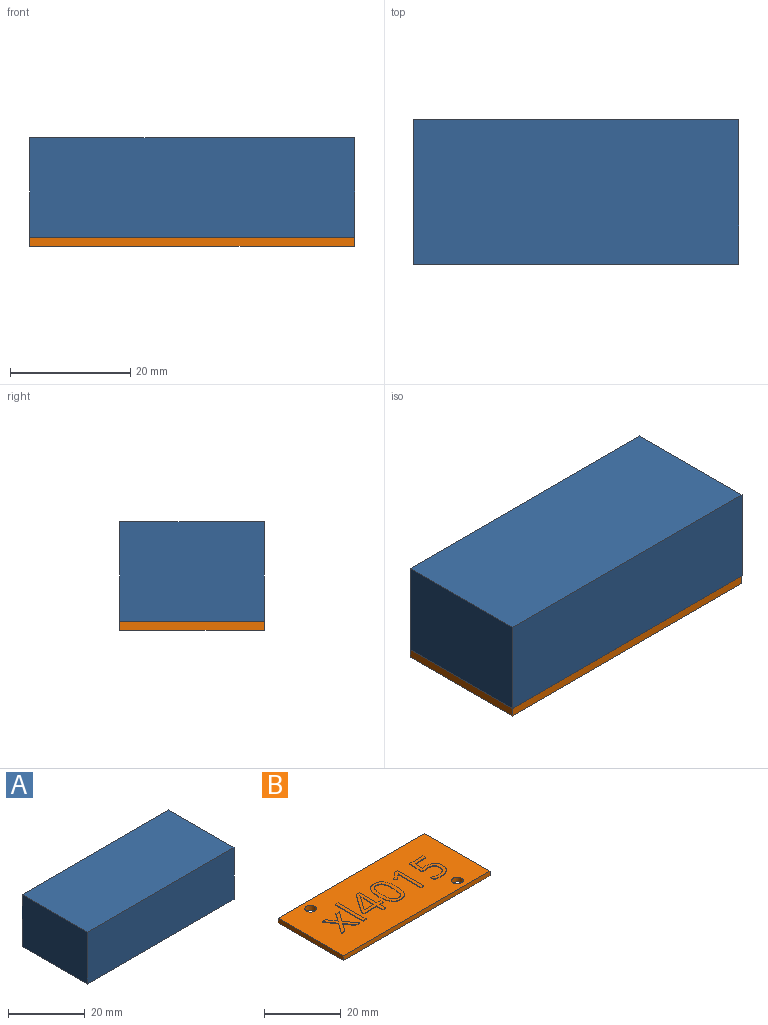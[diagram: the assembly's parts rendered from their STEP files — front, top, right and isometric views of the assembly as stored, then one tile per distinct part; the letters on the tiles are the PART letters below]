
ASSEMBLY  parts=2 mates=1
PART A: 6 faces, bbox 54x24x16.5 mm
  f0: plane 54x16.5mm, normal (0,-1,0), area 891mm2, adj f1,f3,f4,f5
  f1: plane 24x16.5mm, normal (1,0,0), area 396mm2, adj f0,f2,f4,f5
  f2: plane 54x16.5mm, normal (0,1,0), area 891mm2, adj f1,f3,f4,f5
  f3: plane 24x16.5mm, normal (-1,0,0), area 396mm2, adj f0,f2,f4,f5
  f4: plane 54x24mm, normal (0,0,1), area 1296mm2, adj f0,f1,f2,f3
  f5: plane 54x24mm, normal (0,0,-1), area 1296mm2, adj f0,f1,f2,f3
PART B: 93 faces, bbox 54x24x1.7 mm
  f0: plane 54x24mm, normal (0,0,1), area 1136.2mm2, adj f1,f2,f3,f4,f5,f6,f8,f9
  f1: plane 54x1.5mm, normal (0,-1,0), area 81mm2, adj f0,f2,f6,f7
  f2: plane 24x1.5mm, normal (1,0,0), area 36mm2, adj f0,f1,f3,f7
  f3: plane 54x1.5mm, normal (0,1,0), area 81mm2, adj f0,f2,f6,f7
  f4: cylinder r=1.5mm len=3mm, axis (0,0,-1), area 14.1mm2, adj f0,f7
  f5: cylinder r=1.5mm len=3mm, axis (0,0,-1), area 14.1mm2, adj f0,f7
  f6: plane 24x1.5mm, normal (-1,0,0), area 36mm2, adj f0,f1,f3,f7
  f7: plane 54x24mm, normal (0,0,-1), area 1281.9mm2, adj f1,f2,f3,f4,f5,f6
  f8: plane 3.69x2.64mm, normal (-0.81,0.58,0), area 0.9mm2, adj f0,f9,f19,f20
  f9: plane 1.24x0.2mm, normal (0,-1,0), area 0.2mm2, adj f0,f8,f10,f20
  f10: plane 2.92x2.04mm, normal (0.82,-0.57,0), area 0.7mm2, adj f0,f9,f11,f20
  f11: plane 2.92x2.02mm, normal (-0.82,-0.57,0), area 0.7mm2, adj f0,f10,f12,f20
  f12: plane 1.24x0.2mm, normal (0,-1,0), area 0.2mm2, adj f0,f11,f13,f20
  f13: plane 3.69x2.64mm, normal (0.81,0.58,0), area 0.9mm2, adj f0,f12,f14,f20
  f14: plane 3.52x2.51mm, normal (0.81,-0.58,0), area 0.9mm2, adj f0,f13,f15,f20
  f15: plane 1.23x0.2mm, normal (0,1,0), area 0.2mm2, adj f0,f14,f16,f20
  f16: plane 2.76x1.89mm, normal (-0.82,0.57,0), area 0.7mm2, adj f0,f15,f17,f20
  f17: plane 2.76x1.9mm, normal (0.82,0.57,0), area 0.7mm2, adj f0,f16,f18,f20
  f18: plane 1.24x0.2mm, normal (0,1,0), area 0.2mm2, adj f0,f17,f19,f20
  f19: plane 3.52x2.51mm, normal (-0.81,-0.58,0), area 0.9mm2, adj f0,f8,f18,f20
  f20: plane 7.21x6.53mm, normal (0,0,1), area 16.4mm2, adj f8,f9,f10,f11,f12,f13,f14,f15
  f21: plane 10.23x0.2mm, normal (1,0,0), area 2mm2, adj f0,f22,f24,f25
  f22: plane 1.09x0.2mm, normal (0,1,0), area 0.2mm2, adj f0,f21,f23,f25
  f23: plane 10.23x0.2mm, normal (-1,0,0), area 2mm2, adj f0,f22,f24,f25
  f24: plane 1.09x0.2mm, normal (0,-1,0), area 0.2mm2, adj f0,f21,f23,f25
  f25: plane 10.23x1.09mm, normal (0,0,1), area 11.2mm2, adj f21,f22,f23,f24
  f26: plane 0.99x0.2mm, normal (1,0,0), area 0.2mm2, adj f0,f27,f42,f43
  f27: plane 1.43x0.2mm, normal (0,1,0), area 0.3mm2, adj f0,f26,f28,f43
  f28: plane 6.47x0.2mm, normal (1,0,0), area 1.3mm2, adj f0,f27,f29,f43
  f29: plane 1.16x0.2mm, normal (0,1,0), area 0.2mm2, adj f0,f28,f30,f43
  f30: plane 6.51x4.56mm, normal (-0.82,0.57,0), area 1.6mm2, adj f0,f29,f31,f43
  f31: plane 0.95x0.2mm, normal (-1,0,0), area 0.2mm2, adj f0,f30,f32,f43
  f32: plane 4.68x0.2mm, normal (0,-1,0), area 0.9mm2, adj f0,f31,f33,f43
  f33: plane 2.21x0.2mm, normal (-1,0,0), area 0.4mm2, adj f0,f32,f34,f43
  f34: plane 1.05x0.2mm, normal (0,-1,0), area 0.2mm2, adj f0,f33,f35,f43
  f35: plane 2.21x0.2mm, normal (1,0,0), area 0.4mm2, adj f0,f34,f42,f43
  f36: plane 3.58x0.2mm, normal (0,1,0), area 0.7mm2, adj f37,f41,f43,f44
  f37: plane 4.27x3.01mm, normal (0.82,-0.58,0), area 1mm2, adj f36,f38,f43,f44
  f38: extruded ~1.05x0.59mm, area 0.2mm2, adj f37,f39,f43,f44
  f39: plane 0.2x0.05mm, normal (0,-1,0), area 0mm2, adj f38,f40,f43,f44
  f40: extruded ~2.12x0.2mm, area 0.4mm2, adj f39,f41,f43,f44
  f41: plane 3.2x0.2mm, normal (-1,0,0), area 0.6mm2, adj f36,f40,f43,f44
  f42: plane 1.43x0.2mm, normal (0,-1,0), area 0.3mm2, adj f0,f26,f35,f43
  f43: plane 9.67x7.15mm, normal (0,0,1), area 22.3mm2, adj f26,f27,f28,f29,f30,f31,f32,f33
  f44: plane 5.32x3.65mm, normal (0,0,1), area 9.2mm2, adj f36,f37,f38,f39,f40,f41
  f45: extruded ~3.68x0.81mm, area 0.8mm2, adj f0,f46,f60,f61
  f46: extruded ~2.38x1.27mm, area 0.6mm2, adj f0,f45,f47,f61
  f47: extruded ~2.39x1.22mm, area 0.6mm2, adj f0,f46,f48,f61
  f48: extruded ~3.73x0.78mm, area 0.8mm2, adj f0,f47,f49,f61
  f49: extruded ~3.69x0.81mm, area 0.8mm2, adj f0,f48,f50,f61
  f50: extruded ~2.36x1.26mm, area 0.6mm2, adj f0,f49,f51,f61
  f51: extruded ~2.4x1.23mm, area 0.6mm2, adj f0,f50,f60,f61
  f52: extruded ~3.05x0.49mm, area 0.6mm2, adj f53,f59,f61,f62
  f53: extruded ~1.57x0.95mm, area 0.4mm2, adj f52,f54,f61,f62
  f54: extruded ~1.58x0.96mm, area 0.4mm2, adj f53,f55,f61,f62
  f55: extruded ~3.03x0.49mm, area 0.6mm2, adj f54,f56,f61,f62
  f56: extruded ~3.04x0.49mm, area 0.6mm2, adj f55,f57,f61,f62
  f57: extruded ~1.58x0.97mm, area 0.4mm2, adj f56,f58,f61,f62
  f58: extruded ~1.57x0.96mm, area 0.4mm2, adj f57,f59,f61,f62
  f59: extruded ~3.06x0.49mm, area 0.6mm2, adj f52,f58,f61,f62
  f60: extruded ~3.72x0.79mm, area 0.8mm2, adj f0,f45,f51,f61
  f61: plane 9.9x6.36mm, normal (0,0,1), area 24.4mm2, adj f45,f46,f47,f48,f49,f50,f51,f52
  f62: plane 8.01x4.14mm, normal (0,0,1), area 28mm2, adj f52,f53,f54,f55,f56,f57,f58,f59
  f63: plane 9.62x0.2mm, normal (1,0,0), area 1.9mm2, adj f0,f64,f71,f72
  f64: plane 0.92x0.2mm, normal (0,1,0), area 0.2mm2, adj f0,f63,f65,f72
  f65: plane 2.54x1.97mm, normal (-0.61,0.79,0), area 0.6mm2, adj f0,f64,f66,f72
  f66: plane 0.75x0.58mm, normal (-0.79,-0.61,0), area 0.2mm2, adj f0,f65,f67,f72
  f67: extruded ~1.56x1.28mm, area 0.4mm2, adj f0,f66,f68,f72
  f68: extruded ~0.31x0.29mm, area 0.1mm2, adj f0,f67,f69,f72
  f69: extruded ~1.62x0.2mm, area 0.3mm2, adj f0,f68,f70,f72
  f70: plane 6.85x0.2mm, normal (-1,0,0), area 1.4mm2, adj f0,f69,f71,f72
  f71: plane 1.07x0.2mm, normal (0,-1,0), area 0.2mm2, adj f0,f63,f70,f72
  f72: plane 9.62x3.46mm, normal (0,0,1), area 12.7mm2, adj f63,f64,f65,f66,f67,f68,f69,f70
  f73: extruded ~1.51x0.2mm, area 0.3mm2, adj f0,f74,f91,f92
  f74: plane 2.89x0.24mm, normal (1,-0.08,0), area 0.6mm2, adj f0,f73,f75,f92
  f75: plane 3.85x0.2mm, normal (0,-1,0), area 0.8mm2, adj f0,f74,f76,f92
  f76: plane 1.01x0.2mm, normal (1,0,0), area 0.2mm2, adj f0,f75,f77,f92
  f77: plane 4.78x0.2mm, normal (0,1,0), area 1mm2, adj f0,f76,f78,f92
  f78: plane 4.5x0.36mm, normal (-1,0.08,0), area 0.9mm2, adj f0,f77,f79,f92
  f79: plane 0.57x0.36mm, normal (-0.54,-0.84,0), area 0.1mm2, adj f0,f78,f80,f92
  f80: extruded ~1.67x0.2mm, area 0.3mm2, adj f0,f79,f81,f92
  f81: extruded ~2.46x2.01mm, area 0.7mm2, adj f0,f80,f82,f92
  f82: extruded ~1.58x0.64mm, area 0.4mm2, adj f0,f81,f83,f92
  f83: extruded ~1.8x0.55mm, area 0.4mm2, adj f0,f82,f84,f92
  f84: extruded ~1.35x0.2mm, area 0.3mm2, adj f0,f83,f85,f92
  f85: extruded ~1.14x0.46mm, area 0.2mm2, adj f0,f84,f86,f92
  f86: plane 1.05x0.2mm, normal (-1,0,0), area 0.2mm2, adj f0,f85,f87,f92
  f87: extruded ~2.48x0.52mm, area 0.5mm2, adj f0,f86,f88,f92
  f88: extruded ~2.62x0.85mm, area 0.6mm2, adj f0,f87,f89,f92
  f89: extruded ~2.34x0.95mm, area 0.5mm2, adj f0,f88,f90,f92
  f90: extruded ~2.06x0.87mm, area 0.5mm2, adj f0,f89,f91,f92
  f91: extruded ~2.39x0.75mm, area 0.5mm2, adj f0,f73,f90,f92
  f92: plane 9.75x6.05mm, normal (0,0,1), area 21.5mm2, adj f73,f74,f75,f76,f77,f78,f79,f80
PLACE A t=(1.67,-0.15,-9.18)mm
PLACE B t=(1.62,-0.14,-9.18)mm
MATE fastened A.f5 <-> B.f62  axis (0,0,-1) through (1.67,-0.15,-7.68)mm
